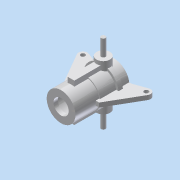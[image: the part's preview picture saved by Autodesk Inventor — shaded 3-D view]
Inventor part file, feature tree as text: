
AUTODESK INVENTOR PART (.ipt)
format: ipt  version: 2011 SP1 (Build 150282100, 282)  size: 228,352 bytes
history: native  units: in
note: dims shown in document units (in); Inventor stores cm internally (conversion verified against a paired STEP export)
features: extrude x10, sketch x10, plane x4, pattern_circular x2, mirror x1
ambient origin geometry x8: Origin, YZ Plane, XZ Plane, XY Plane, X Axis, Y Axis, Z Axis, Center Point
bodies: Solid1 (feature_tree)
feature tree (27):
  extrude  "Extrusion1"  Depth=0.55in TaperAngle=0.0deg
  extrude  "Extrusion2"  Depth=0.67in TaperAngle=0.0deg
  plane  "Work Plane1"
  extrude  "Extrusion3"  Depth=0.81in
  plane  "Work Plane6"
  extrude  "Extrusion4"  Depth=0.18in
  plane  "Work Plane7"
  extrude  "Extrusion5"  Depth=0.05in
  pattern_circular  "Circular Pattern1"  [2 undecoded]
  extrude  "Extrusion6"  Depth=0.1in TaperAngle=0.0deg
  pattern_circular  "Circular Pattern2"  Count=2 Angle=360.0deg
  extrude  "Extrusion7"  Depth=0.1in
  extrude  "Extrusion8"  Depth=0.375in TaperAngle=0.0deg
  extrude  "Extrusion9"  Depth=0.7874in TaperAngle=360.0deg
  extrude  "Extrusion10"  Depth=0.55in
  mirror  "Mirror1"
  sketch  "Sketch2"  dims[d0=0.66in d1=0.55in d2=0.0in]
  sketch  "Sketch3"  dims[d3=0.7in d4=0.67in d5=0.0in]
  sketch  "Sketch4"  dims[d6=-0.37in d7=0.81in]
  plane  "Work Plane5"
  sketch  "Sketch6"  dims[d8=0.1in d9=0.0in d15=0.18in]
  sketch  "Sketch7"  dims[d16=0.31in d17=0.05in]
  sketch  "Sketch8"  dims[d18=0.1in d19=0.0in]
  sketch  "Sketch9"  dims[d20=-0.23in]
  sketch  "Sketch10"  dims[d25=0.66in]
  sketch  "Sketch12"  dims[d26=0.15in]
  sketch  "Sketch13"  dims[d27=0.12in d28=0.075in d29=0.1in d30=0.0in d31=0.7874in d32=360.0deg d34=0.1in d35=0.375in d36=0.0in d37=0.7874in d38=360.0deg d40=0.55in d41=1.12in d42=0.0in d43=0.35in d44=1.12in d45=0.0in d46=0.1in d47=0.2in d48=30.0deg d49=0.75in d50=0.1in d51=0.0in d52=0.1in d53=0.0in]
note: 2 required parameter values undecoded (feature->parameter linkage not recoverable at this tier; creation-order binding heuristic only, values carry confidence <= 0.55)
